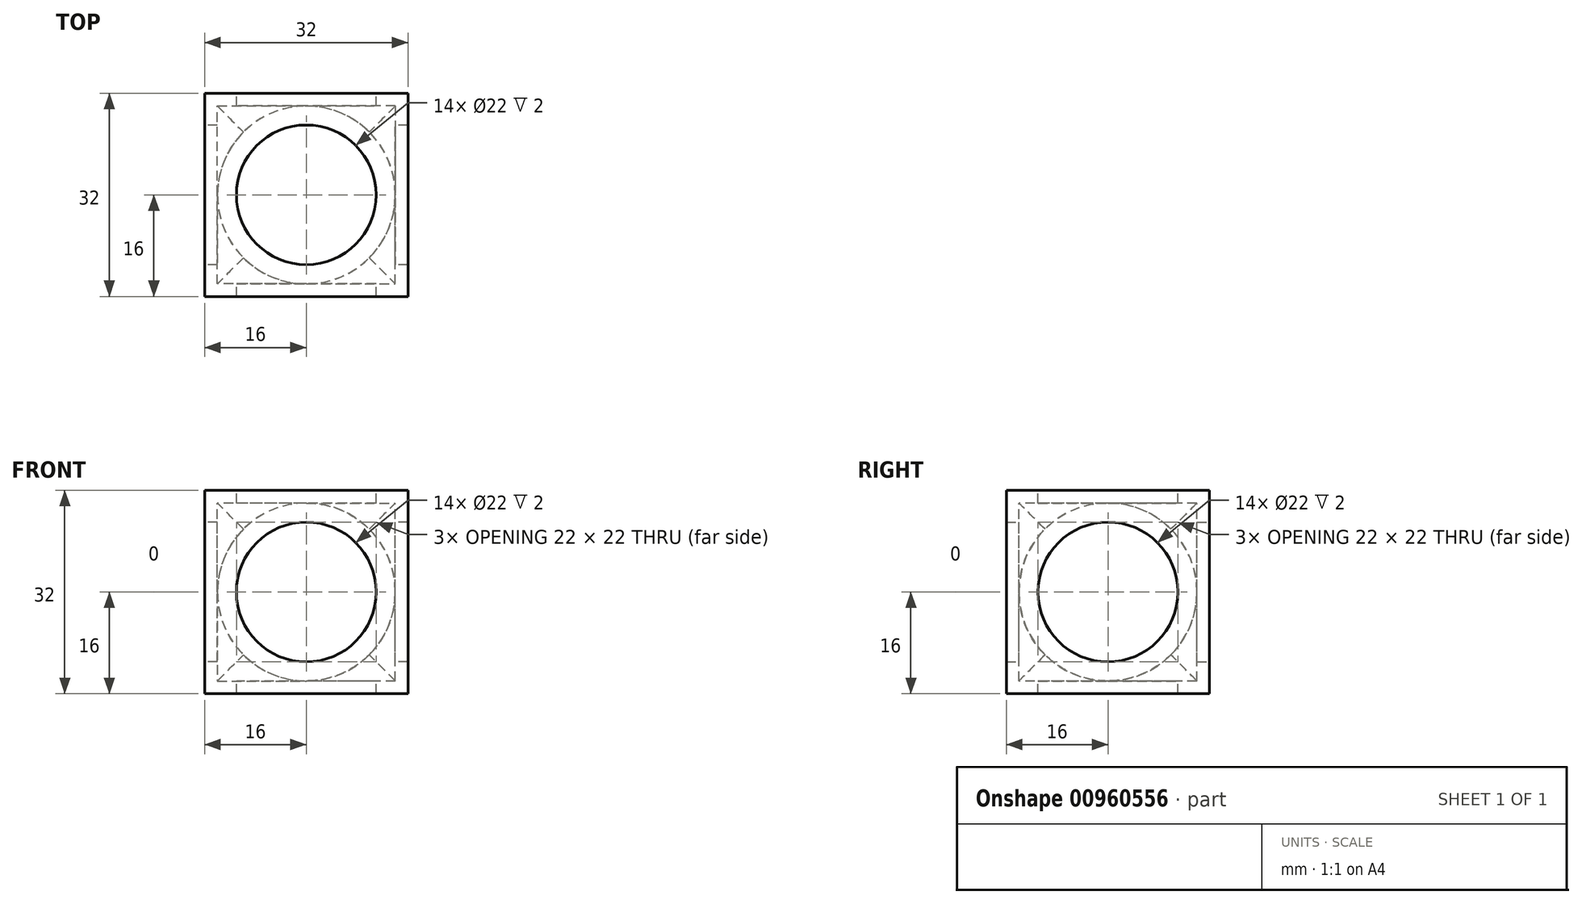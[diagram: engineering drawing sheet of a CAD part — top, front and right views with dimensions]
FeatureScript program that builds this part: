
annotation { "Feature Type Name" : "Feature", "Feature Type Description" : "" }
export const myFeature = defineFeature(function(context is Context, id is Id, definition is map)
    precondition{}
    {
        {
            var Q0;
            Q0=qCreatedBy(makeId("Top.planeOp"),FACE);
            var sketch = newSketch(context, id + "F0", { "sketchPlane" : qUnion([Q0])});
            skLineSegment(sketch, "E0.bottom", {"start": v(16, 16) * mm, "end": v(-16, 16) * mm});
            skLineSegment(sketch, "E0.top", {"start": v(16, -16) * mm, "end": v(-16, -16) * mm});
            skLineSegment(sketch, "E0.left", {"start": v(16, 16) * mm, "end": v(16, -16) * mm});
            skLineSegment(sketch, "E0.right", {"start": v(-16, 16) * mm, "end": v(-16, -16) * mm});
            skPoint(sketch, "E0.middle", {"position": v(0, 0) * mm});
            skSolve(sketch);
        }
        {
            var Q0;
            Q0 = qSketchRegion(id + "F0", true);
            extrude(context, id + "F1", {"entities" : qUnion([Q0]), "endBound" : BoundingType.SYMMETRIC, "depth" : 32 * mm, "offsetDistance" : 25 * mm});
        }
        {
            var Q0;
            Q0=makeQuery(id+"F1.opExtrude","CAP_FACE",FACE,{"disambiguationData":[OSD([sQuery(id+"F0.wireOp",EDGE,"E0.bottom"),sQuery(id+"F0.wireOp",EDGE,"E0.top"),sQuery(id+"F0.wireOp",EDGE,"E0.left"),sQuery(id+"F0.wireOp",EDGE,"E0.right")])],"isStart":false});
            var sketch = newSketch(context, id + "F2", { "sketchPlane" : qUnion([Q0])});
            skCircle(sketch, "E1", {"center": v(0, 0) * mm, "radius": 11 * mm});
            skSolve(sketch);
        }
        {
            var Q0;
            Q0 = qSketchRegion(id + "F2", true);
            extrude(context, id + "F3", {"entities" : qUnion([Q0]), "operationType" : NewBodyOperationType.REMOVE, "endBound" : BoundingType.THROUGH_ALL, "oppositeDirection" : true, "depth" : 25 * mm, "offsetDistance" : 25 * mm});
        }
        {
            var Q0;
            Q0=makeQuery(id+"F1.opExtrude","SWEPT_FACE",FACE,{"disambiguationData":[OSD([sQuery(id+"F0.wireOp",EDGE,"E0.bottom")])]});
            var sketch = newSketch(context, id + "F4", { "sketchPlane" : qUnion([Q0])});
            skCircle(sketch, "E2", {"center": v(0, 0) * mm, "radius": 11 * mm});
            skSolve(sketch);
        }
        {
            var Q0;
            Q0 = qSketchRegion(id + "F4", true);
            extrude(context, id + "F5", {"entities" : qUnion([Q0]), "operationType" : NewBodyOperationType.REMOVE, "endBound" : BoundingType.THROUGH_ALL, "oppositeDirection" : true, "depth" : 25 * mm, "offsetDistance" : 25 * mm});
        }
        {
            var Q0;
            Q0=makeQuery(id+"F1.opExtrude","SWEPT_FACE",FACE,{"disambiguationData":[OSD([sQuery(id+"F0.wireOp",EDGE,"E0.right")])]});
            var sketch = newSketch(context, id + "F6", { "sketchPlane" : qUnion([Q0])});
            skCircle(sketch, "E3", {"center": v(0, 0) * mm, "radius": 11 * mm});
            skSolve(sketch);
        }
        {
            var Q0;
            Q0 = qSketchRegion(id + "F6", true);
            extrude(context, id + "F7", {"entities" : qUnion([Q0]), "operationType" : NewBodyOperationType.REMOVE, "endBound" : BoundingType.THROUGH_ALL, "oppositeDirection" : true, "depth" : 25 * mm, "offsetDistance" : 25 * mm});
        }
        {
            var Q0;
            Q0=qCreatedBy(makeId("Top.planeOp"),FACE);
            var sketch = newSketch(context, id + "F8", { "sketchPlane" : qUnion([Q0])});
            skCircle(sketch, "E4", {"center": v(0, 0) * mm, "radius": 14 * mm});
            skSolve(sketch);
        }
        {
            var Q0;
            Q0 = qSketchRegion(id + "F8", true);
            extrude(context, id + "F9", {"entities" : qUnion([Q0]), "operationType" : NewBodyOperationType.REMOVE, "endBound" : BoundingType.SYMMETRIC, "oppositeDirection" : true, "depth" : 28 * mm, "offsetDistance" : 25 * mm});
        }
        {
            var Q0;
            Q0=qCreatedBy(makeId("Front.planeOp"),FACE);
            var sketch = newSketch(context, id + "F10", { "sketchPlane" : qUnion([Q0])});
            skCircle(sketch, "E5", {"center": v(0, 0) * mm, "radius": 14 * mm});
            skSolve(sketch);
        }
        {
            var Q0;
            Q0 = qSketchRegion(id + "F10", true);
            extrude(context, id + "F11", {"entities" : qUnion([Q0]), "operationType" : NewBodyOperationType.REMOVE, "endBound" : BoundingType.SYMMETRIC, "oppositeDirection" : true, "depth" : 28 * mm, "offsetDistance" : 25 * mm});
        }
        {
            var Q0;
            Q0=qCreatedBy(makeId("Right.planeOp"),FACE);
            var sketch = newSketch(context, id + "F12", { "sketchPlane" : qUnion([Q0])});
            skCircle(sketch, "E6", {"center": v(0, 0) * mm, "radius": 14 * mm});
            skSolve(sketch);
        }
        {
            var Q0;
            Q0 = qSketchRegion(id + "F12", true);
            extrude(context, id + "F13", {"entities" : qUnion([Q0]), "operationType" : NewBodyOperationType.REMOVE, "endBound" : BoundingType.SYMMETRIC, "depth" : 28 * mm, "offsetDistance" : 25 * mm});
        }
    });
